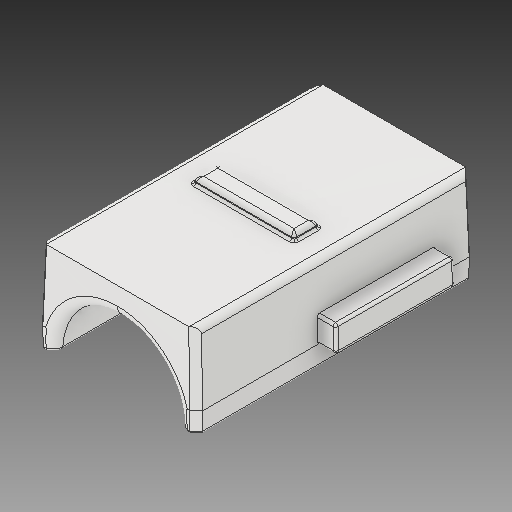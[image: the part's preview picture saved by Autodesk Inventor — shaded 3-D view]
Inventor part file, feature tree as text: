
AUTODESK INVENTOR PART (.ipt)
format: ipt  version: 2019 (Build 230136000, 136)  size: 429,056 bytes
history: native  units: in
note: dims shown in document units (in); Inventor stores cm internally (conversion verified against a paired STEP export)
features: fillet x1
ambient origin geometry x8: Origin, YZ Plane, XZ Plane, XY Plane, X Axis, Y Axis, Z Axis, Center Point
bodies: Solid1 (feature_tree)
feature tree (1):
  fillet  "Fillet17"  [1 undecoded]
note: 1 required parameter value undecoded (feature->parameter linkage not recoverable at this tier; creation-order binding heuristic only, values carry confidence <= 0.55)
